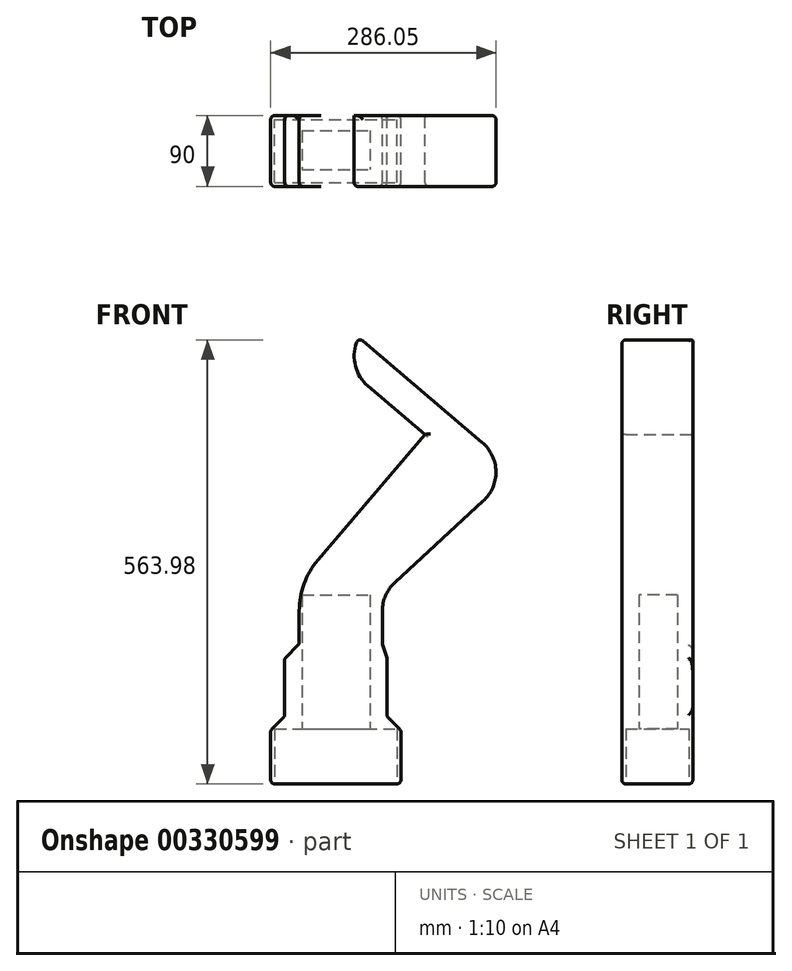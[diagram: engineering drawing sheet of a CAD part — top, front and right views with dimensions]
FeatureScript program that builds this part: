
annotation { "Feature Type Name" : "Feature", "Feature Type Description" : "" }
export const myFeature = defineFeature(function(context is Context, id is Id, definition is map)
    precondition{}
    {
        {
            var Q0;
            Q0=qCreatedBy(makeId("Front.planeOp"),FACE);
            var sketch = newSketch(context, id + "F0", { "sketchPlane" : qUnion([Q0])});
            skLineSegment(sketch, "E0", {"start": v(-126.26, -261.83) * mm, "end": v(39.1, -261.83) * mm});
            skLineSegment(sketch, "E1", {"start": v(21.42, -176.02) * mm, "end": v(39.1, -193.7) * mm});
            skLineSegment(sketch, "E2", {"start": v(39.1, -193.7) * mm, "end": v(39.1, -261.83) * mm});
            skLineSegment(sketch, "E3", {"start": v(-126.26, -261.83) * mm, "end": v(-126.26, -193.7) * mm});
            skLineSegment(sketch, "E4", {"start": v(-126.26, -193.7) * mm, "end": v(-108.58, -176.02) * mm});
            skLineSegment(sketch, "E5", {"start": v(-108.58, -176.02) * mm, "end": v(-108.58, -102.66) * mm});
            skLineSegment(sketch, "E6", {"start": v(-108.58, -102.66) * mm, "end": v(-90.06, -84.13) * mm});
            skLineSegment(sketch, "E7", {"start": v(-90.06, -84.13) * mm, "end": v(-90.06, -42.2) * mm});
            skArc(sketch, "E8", {"start": v(-66.27, 22.5) * mm, "mid": v(-83.92, -7.73) * mm, "end": v(-90.06, -42.2) * mm});
            skLineSegment(sketch, "E9", {"start": v(-66.27, 22.5) * mm, "end": v(69.5, 182.23) * mm});
            skLineSegment(sketch, "E10", {"start": v(69.5, 182.23) * mm, "end": v(-66.27, 297.63) * mm});
            skLineSegment(sketch, "E11", {"start": v(21.42, -176.02) * mm, "end": v(21.42, -102.66) * mm});
            skLineSegment(sketch, "E12", {"start": v(15.55, -84.13) * mm, "end": v(21.42, -102.66) * mm});
            skLineSegment(sketch, "E13", {"start": v(15.55, -84.13) * mm, "end": v(15.55, -42.2) * mm});
            skArc(sketch, "E14", {"start": v(31.4, -6.07) * mm, "mid": v(19.69, -22.47) * mm, "end": v(15.55, -42.2) * mm});
            skLineSegment(sketch, "E15", {"start": v(31.4, -6.07) * mm, "end": v(185.23, 135.56) * mm});
            skLineSegment(sketch, "E16", {"start": v(185.23, 135.56) * mm, "end": v(-14.42, 305.27) * mm});
            skLineSegment(sketch, "E17", {"start": v(-14.42, 305.27) * mm, "end": v(-66.27, 297.63) * mm});
            skArc(sketch, "E18", {"start": v(46.03, 154.62) * mm, "mid": v(23.87, 206.79) * mm, "end": v(-11.5, 251.07) * mm});
            skSolve(sketch);
        }
        {
            var Q0;
            Q0=makeQuery(id+"F0.imprint","IMPRINT",FACE,{"disambiguationData":[TD([[makeQuery(id+"F0.imprint","IMPRINT",EDGE,{"derivedFrom":sQuery(id+"F0.wireOp",EDGE,"E0")}),1.0]])]});
            extrude(context, id + "F1", {"entities" : qUnion([Q0]), "depth" : 90 * mm});
        }
        {
            var Q0;
            Q0=makeQuery(id+"F1.opExtrude","SWEPT_EDGE",EDGE,{"disambiguationData":[OSD([sQuery(id+"F0.wireOp",EDGE,"E10"),sQuery(id+"F0.wireOp",EDGE,"E17")])]});
            var Q1;
            Q1=makeQuery(id+"F1.opExtrude","SWEPT_EDGE",EDGE,{"disambiguationData":[OSD([sQuery(id+"F0.wireOp",EDGE,"E15"),sQuery(id+"F0.wireOp",EDGE,"E16")])]});
            fillet(context, id + "F2", {"entities" : qUnion([Q0, Q1]), "radius" : 50 * mm, "tangentPropagation" : true, "allowEdgeOverflow" : false});
        }
        {
            var Q0;
            Q0=makeQuery(id+"F1.opExtrude","SWEPT_FACE",FACE,{"disambiguationData":[OSD([sQuery(id+"F0.wireOp",EDGE,"E1")])]});
            var Q1;
            Q1=makeQuery(id+"F1.opExtrude","CAP_EDGE",EDGE,{"disambiguationData":[OSD([sQuery(id+"F0.wireOp",EDGE,"E5")])],"isStart":true});
            var Q2;
            Q2=makeQuery(id+"F1.opExtrude","SWEPT_FACE",FACE,{"disambiguationData":[OSD([sQuery(id+"F0.wireOp",EDGE,"E4")])]});
            var Q3;
            Q3=makeQuery(id+"F1.opExtrude","SWEPT_FACE",FACE,{"disambiguationData":[OSD([sQuery(id+"F0.wireOp",EDGE,"E3")])]});
            var Q4;
            Q4=makeQuery(id+"F1.opExtrude","SWEPT_EDGE",EDGE,{"disambiguationData":[OSD([sQuery(id+"F0.wireOp",EDGE,"E5"),sQuery(id+"F0.wireOp",EDGE,"E6")])]});
            var Q5;
            Q5=makeQuery(id+"F1.opExtrude","SWEPT_FACE",FACE,{"disambiguationData":[OSD([sQuery(id+"F0.wireOp",EDGE,"E7")])]});
            var Q6;
            Q6=makeQuery(id+"F1.opExtrude","SWEPT_FACE",FACE,{"disambiguationData":[OSD([sQuery(id+"F0.wireOp",EDGE,"E8")])]});
            var Q7;
            Q7=makeQuery(id+"F1.opExtrude","SWEPT_FACE",FACE,{"disambiguationData":[OSD([sQuery(id+"F0.wireOp",EDGE,"E16")])]});
            var Q8;
            Q8=makeQuery(id+"F1.opExtrude","SWEPT_FACE",FACE,{"disambiguationData":[OSD([sQuery(id+"F0.wireOp",EDGE,"E2")])]});
            var Q9;
            Q9=makeQuery(id+"F1.opExtrude","CAP_EDGE",EDGE,{"disambiguationData":[OSD([sQuery(id+"F0.wireOp",EDGE,"E0")])],"isStart":true});
            var Q10;
            Q10=makeQuery(id+"F1.opExtrude","CAP_FACE",FACE,{"disambiguationData":[OSD([sQuery(id+"F0.wireOp",EDGE,"E0"),sQuery(id+"F0.wireOp",EDGE,"E1"),sQuery(id+"F0.wireOp",EDGE,"E2"),sQuery(id+"F0.wireOp",EDGE,"E3"),sQuery(id+"F0.wireOp",EDGE,"E4"),sQuery(id+"F0.wireOp",EDGE,"E5"),sQuery(id+"F0.wireOp",EDGE,"E6"),sQuery(id+"F0.wireOp",EDGE,"E7"),sQuery(id+"F0.wireOp",EDGE,"E8"),sQuery(id+"F0.wireOp",EDGE,"E9"),sQuery(id+"F0.wireOp",EDGE,"E10"),sQuery(id+"F0.wireOp",EDGE,"E11"),sQuery(id+"F0.wireOp",EDGE,"E12"),sQuery(id+"F0.wireOp",EDGE,"E13"),sQuery(id+"F0.wireOp",EDGE,"E14"),sQuery(id+"F0.wireOp",EDGE,"E15"),sQuery(id+"F0.wireOp",EDGE,"E16"),sQuery(id+"F0.wireOp",EDGE,"E17")])],"isStart":false});
            var Q11;
            Q11=makeQuery(id+"F1.opExtrude","SWEPT_FACE",FACE,{"disambiguationData":[OSD([sQuery(id+"F0.wireOp",EDGE,"E12")])]});
            fillet(context, id + "F3", {"entities" : qUnion([Q0, Q1, Q2, Q3, Q4, Q5, Q6, Q7, Q8, Q9, Q10, Q11]), "radius" : 5 * mm, "tangentPropagation" : true, "allowEdgeOverflow" : false});
        }
        {
            var Q0;
            Q0=makeQuery(id+"F1.opExtrude","SWEPT_FACE",FACE,{"disambiguationData":[OSD([sQuery(id+"F0.wireOp",EDGE,"E0")])]});
            extrude(context, id + "F4", {"entities" : qUnion([Q0]), "operationType" : NewBodyOperationType.REMOVE, "oppositeDirection" : true, "depth" : 70 * mm});
        }
        {
            var Q0;
            Q0=makeQuery(id+"F4.boolean.opBoolean","COPY",FACE,{"derivedFrom":makeQuery(id+"F4.opExtrude","CAP_FACE",FACE,{"disambiguationData":[OSD([sQuery(id+"F0.wireOp",EDGE,"E0")])],"isStart":false})});
            var sketch = newSketch(context, id + "F5", { "sketchPlane" : qUnion([Q0])});
            skLineSegment(sketch, "E19.bottom", {"start": v(-86.51, 19.23) * mm, "end": v(0, 19.23) * mm});
            skLineSegment(sketch, "E19.top", {"start": v(-86.51, 68.5) * mm, "end": v(0, 68.5) * mm});
            skLineSegment(sketch, "E19.left", {"start": v(-86.51, 19.23) * mm, "end": v(-86.51, 68.5) * mm});
            skLineSegment(sketch, "E19.right", {"start": v(0, 19.23) * mm, "end": v(0, 68.5) * mm});
            skSolve(sketch);
        }
        {
            var Q0;
            Q0=makeQuery(id+"F5.imprint","IMPRINT",FACE,{"disambiguationData":[TD([[makeQuery(id+"F5.imprint","IMPRINT",EDGE,{"derivedFrom":sQuery(id+"F5.wireOp",EDGE,"E19.bottom")}),1.0]])]});
            extrude(context, id + "F6", {"entities" : qUnion([Q0]), "operationType" : NewBodyOperationType.REMOVE, "oppositeDirection" : true, "depth" : 170 * mm});
        }
    });
